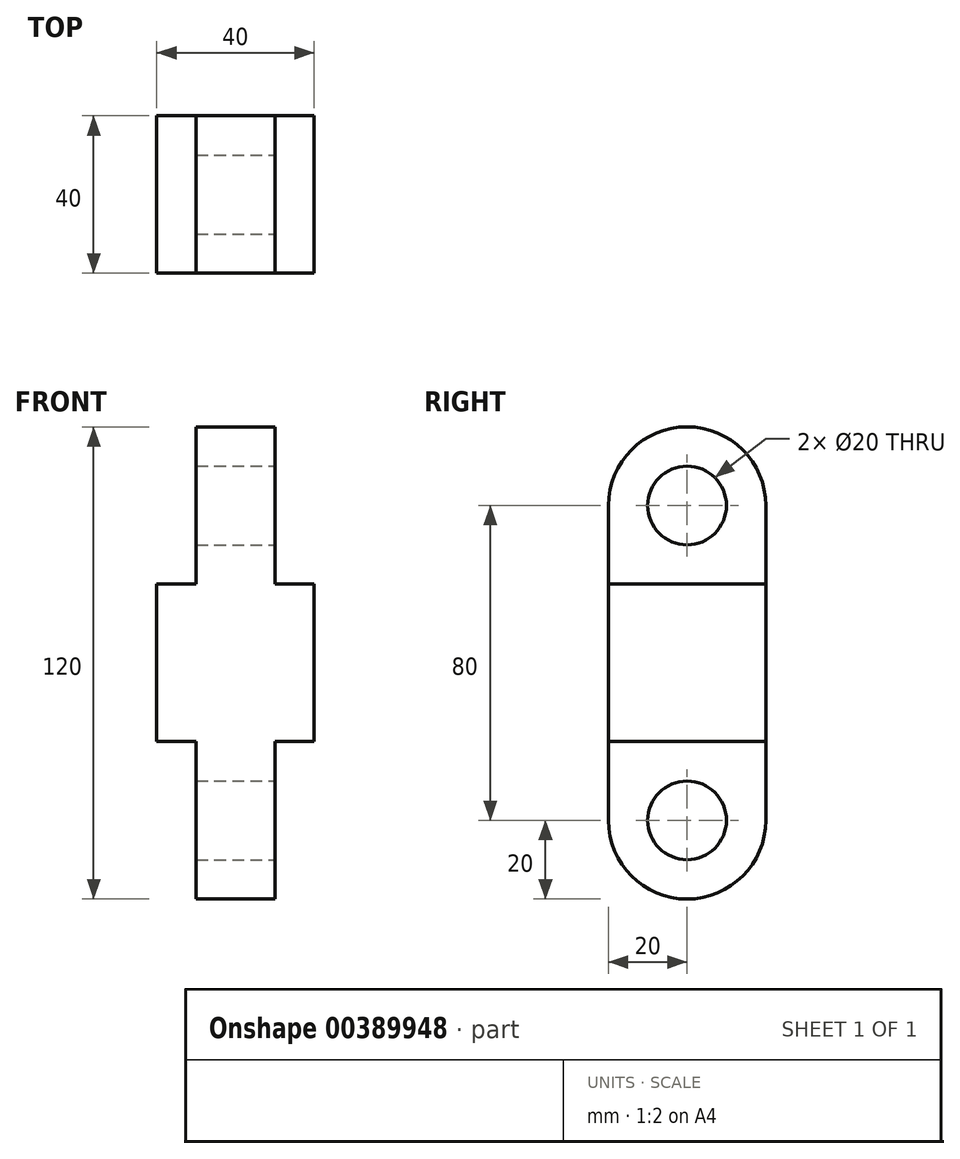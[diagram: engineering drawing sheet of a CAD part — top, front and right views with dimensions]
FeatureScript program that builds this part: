
annotation { "Feature Type Name" : "Feature", "Feature Type Description" : "" }
export const myFeature = defineFeature(function(context is Context, id is Id, definition is map)
    precondition{}
    {
        {
            var Q0;
            Q0=qCreatedBy(makeId("Front.planeOp"),FACE);
            var sketch = newSketch(context, id + "F0", { "sketchPlane" : qUnion([Q0])});
            skLineSegment(sketch, "E0.bottom", {"start": v(20, -60) * mm, "end": v(-20, -60) * mm});
            skLineSegment(sketch, "E0.top", {"start": v(20, 60) * mm, "end": v(-20, 60) * mm});
            skLineSegment(sketch, "E0.left", {"start": v(20, -60) * mm, "end": v(20, 60) * mm});
            skLineSegment(sketch, "E0.right", {"start": v(-20, -60) * mm, "end": v(-20, 60) * mm});
            skPoint(sketch, "E0.middle", {"position": v(0, 0) * mm});
            skSolve(sketch);
        }
        {
            var Q0;
            Q0 = qSketchRegion(id + "F0", true);
            extrude(context, id + "F1", {"entities" : qUnion([Q0]), "depth" : 40 * mm});
        }
        {
            var Q0;
            Q0=makeQuery(id+"F1.opExtrude","CAP_FACE",FACE,{"disambiguationData":[OSD([sQuery(id+"F0.wireOp",EDGE,"E0.bottom"),sQuery(id+"F0.wireOp",EDGE,"E0.top"),sQuery(id+"F0.wireOp",EDGE,"E0.left"),sQuery(id+"F0.wireOp",EDGE,"E0.right")])],"isStart":false});
            var sketch = newSketch(context, id + "F2", { "sketchPlane" : qUnion([Q0])});
            skLineSegment(sketch, "E1.bottom", {"start": v(-20, 60) * mm, "end": v(-10, 60) * mm});
            skLineSegment(sketch, "E1.top", {"start": v(-20, 20) * mm, "end": v(-10, 20) * mm});
            skLineSegment(sketch, "E1.left", {"start": v(-20, 60) * mm, "end": v(-20, 20) * mm});
            skLineSegment(sketch, "E1.right", {"start": v(-10, 60) * mm, "end": v(-10, 20) * mm});
            skSolve(sketch);
        }
        {
            var Q0;
            Q0 = qSketchRegion(id + "F2", true);
            extrude(context, id + "F3", {"entities" : qUnion([Q0]), "operationType" : NewBodyOperationType.REMOVE, "oppositeDirection" : true, "depth" : 40 * mm});
        }
        {
            var Q0;
            Q0=makeQuery(id+"F1.opExtrude","CAP_FACE",FACE,{"disambiguationData":[OSD([sQuery(id+"F0.wireOp",EDGE,"E0.bottom"),sQuery(id+"F0.wireOp",EDGE,"E0.top"),sQuery(id+"F0.wireOp",EDGE,"E0.left"),sQuery(id+"F0.wireOp",EDGE,"E0.right")])],"isStart":false});
            var sketch = newSketch(context, id + "F4", { "sketchPlane" : qUnion([Q0])});
            skLineSegment(sketch, "E2.bottom", {"start": v(20, 60) * mm, "end": v(10, 60) * mm});
            skLineSegment(sketch, "E2.top", {"start": v(20, 20) * mm, "end": v(10, 20) * mm});
            skLineSegment(sketch, "E2.left", {"start": v(20, 60) * mm, "end": v(20, 20) * mm});
            skLineSegment(sketch, "E2.right", {"start": v(10, 60) * mm, "end": v(10, 20) * mm});
            skSolve(sketch);
        }
        {
            var Q0;
            Q0 = qSketchRegion(id + "F4", true);
            extrude(context, id + "F5", {"entities" : qUnion([Q0]), "operationType" : NewBodyOperationType.REMOVE, "oppositeDirection" : true, "depth" : 40 * mm});
        }
        {
            var Q0;
            Q0=makeQuery(id+"F1.opExtrude","CAP_FACE",FACE,{"disambiguationData":[OSD([sQuery(id+"F0.wireOp",EDGE,"E0.bottom"),sQuery(id+"F0.wireOp",EDGE,"E0.top"),sQuery(id+"F0.wireOp",EDGE,"E0.left"),sQuery(id+"F0.wireOp",EDGE,"E0.right")])],"isStart":false});
            var sketch = newSketch(context, id + "F6", { "sketchPlane" : qUnion([Q0])});
            skLineSegment(sketch, "E3.bottom", {"start": v(-20, -60) * mm, "end": v(-10, -60) * mm});
            skLineSegment(sketch, "E3.top", {"start": v(-20, -20) * mm, "end": v(-10, -20) * mm});
            skLineSegment(sketch, "E3.left", {"start": v(-20, -60) * mm, "end": v(-20, -20) * mm});
            skLineSegment(sketch, "E3.right", {"start": v(-10, -60) * mm, "end": v(-10, -20) * mm});
            skLineSegment(sketch, "E4.bottom", {"start": v(20, -60) * mm, "end": v(10, -60) * mm});
            skLineSegment(sketch, "E4.top", {"start": v(20, -20) * mm, "end": v(10, -20) * mm});
            skLineSegment(sketch, "E4.left", {"start": v(20, -60) * mm, "end": v(20, -20) * mm});
            skLineSegment(sketch, "E4.right", {"start": v(10, -60) * mm, "end": v(10, -20) * mm});
            skSolve(sketch);
        }
        {
            var Q0;
            Q0 = qSketchRegion(id + "F6", true);
            extrude(context, id + "F7", {"entities" : qUnion([Q0]), "operationType" : NewBodyOperationType.REMOVE, "oppositeDirection" : true, "depth" : 40 * mm});
        }
        {
            var Q0;
            Q0=makeQuery(id+"F5.boolean.opBoolean","COPY",FACE,{"derivedFrom":makeQuery(id+"F5.opExtrude","SWEPT_FACE",FACE,{"disambiguationData":[OSD([sQuery(id+"F4.wireOp",EDGE,"E2.right")])]})});
            var sketch = newSketch(context, id + "F8", { "sketchPlane" : qUnion([Q0])});
            skLineSegment(sketch, "E5", {"start": v(-20, 60) * mm, "end": v(-20, 40) * mm, "construction": true});
            skCircle(sketch, "E6", {"center": v(-20, 40) * mm, "radius": 10 * mm});
            skSolve(sketch);
        }
        {
            var Q0;
            Q0 = qSketchRegion(id + "F8", true);
            extrude(context, id + "F9", {"entities" : qUnion([Q0]), "operationType" : NewBodyOperationType.REMOVE, "oppositeDirection" : true, "depth" : 25 * mm});
        }
        {
            var Q0;
            Q0=makeQuery(id+"F7.boolean.opBoolean","COPY",FACE,{"derivedFrom":makeQuery(id+"F7.opExtrude","SWEPT_FACE",FACE,{"disambiguationData":[OSD([sQuery(id+"F6.wireOp",EDGE,"E4.right")])]})});
            var sketch = newSketch(context, id + "F10", { "sketchPlane" : qUnion([Q0])});
            skLineSegment(sketch, "E7", {"start": v(-20, -60) * mm, "end": v(-20, -40) * mm, "construction": true});
            skCircle(sketch, "E8", {"center": v(-20, -40) * mm, "radius": 10 * mm});
            skSolve(sketch);
        }
        {
            var Q0;
            Q0 = qSketchRegion(id + "F10", true);
            extrude(context, id + "F11", {"entities" : qUnion([Q0]), "operationType" : NewBodyOperationType.REMOVE, "oppositeDirection" : true, "depth" : 25 * mm});
        }
        {
            var Q0;
            Q0=makeQuery(id+"F1.opExtrude","CAP_EDGE",EDGE,{"disambiguationData":[OSD([sQuery(id+"F0.wireOp",EDGE,"E0.top")])],"isStart":false});
            var Q1;
            Q1=makeQuery(id+"F1.opExtrude","CAP_EDGE",EDGE,{"disambiguationData":[OSD([sQuery(id+"F0.wireOp",EDGE,"E0.top")])],"isStart":true});
            var Q2;
            Q2=makeQuery(id+"F1.opExtrude","CAP_EDGE",EDGE,{"disambiguationData":[OSD([sQuery(id+"F0.wireOp",EDGE,"E0.bottom")])],"isStart":false});
            var Q3;
            Q3=makeQuery(id+"F1.opExtrude","CAP_EDGE",EDGE,{"disambiguationData":[OSD([sQuery(id+"F0.wireOp",EDGE,"E0.bottom")])],"isStart":true});
            fillet(context, id + "F12", {"entities" : qUnion([Q0, Q1, Q2, Q3]), "radius" : 20 * mm, "tangentPropagation" : true, "allowEdgeOverflow" : false});
        }
    });
